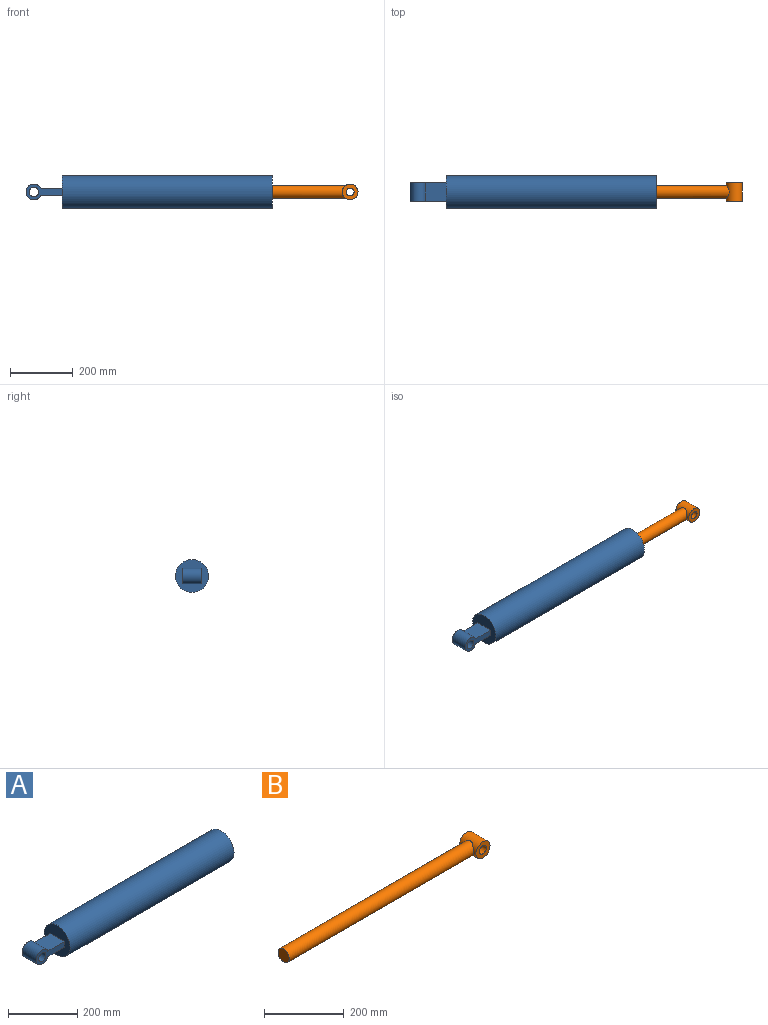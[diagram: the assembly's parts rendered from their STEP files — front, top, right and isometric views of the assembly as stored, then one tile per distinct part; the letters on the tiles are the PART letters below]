
ASSEMBLY  parts=2 mates=1
PART A: 11 faces, bbox 785x105x105 mm
  f0: cylinder r=52.5mm len=670mm, axis (-1,0,0), area 221011mm2, adj f1,f2
  f1: plane 105x105mm, normal (1,0,0), area 7402.4mm2, adj f0,f9
  f2: plane 105x105mm, normal (-1,0,0), area 7499mm2, adj f0,f3,f4,f5,f6
  f3: plane 67.09x58mm, normal (0,0,1), area 3891.1mm2, adj f2,f4,f6,f7
  f4: plane 115x50mm, normal (0,1,0), area 2570.3mm2, adj f2,f3,f5,f7,f8
  f5: plane 67.09x58mm, normal (0,0,-1), area 3891.1mm2, adj f2,f4,f6,f7
  f6: plane 115x50mm, normal (0,-1,0), area 2570.3mm2, adj f2,f3,f5,f7,f8
  f7: cylinder r=25mm len=58mm, axis (0,-1,0), area 7917.2mm2, adj f3,f4,f5,f6
  f8: cylinder r=15mm len=58mm, axis (0,-1,0), area 5466.4mm2, adj f4,f6
  f9: cylinder r=20mm len=650mm, axis (1,0,0), area 81681.4mm2, adj f1,f10
  f10: plane 40x40mm, normal (1,0,0), area 1256.6mm2, adj f9
PART B: 6 faces, bbox 703x58x50 mm
  f0: cylinder r=20mm len=663mm, axis (-1,0,0), area 82646.4mm2, adj f1,f2
  f1: plane 40x40mm, normal (-1,0,0), area 1256.6mm2, adj f0
  f2: cylinder r=25mm len=58mm, axis (0,1,0), area 7715.5mm2, adj f0,f3,f4
  f3: plane 50x50mm, normal (0,-1,0), area 1472.6mm2, adj f2,f5
  f4: plane 50x50mm, normal (0,1,0), area 1472.6mm2, adj f2,f5
  f5: cylinder r=12.5mm len=58mm, axis (0,-1,0), area 4555.3mm2, adj f3,f4
PLACE A t=(-636.35,-341.75,236.79)mm
PLACE B t=(-1066.35,-341.75,236.79)mm
MATE slider B.f0 <-> A.f9  axis (-1,0,0) through (-396.35,-341.75,236.79)mm
